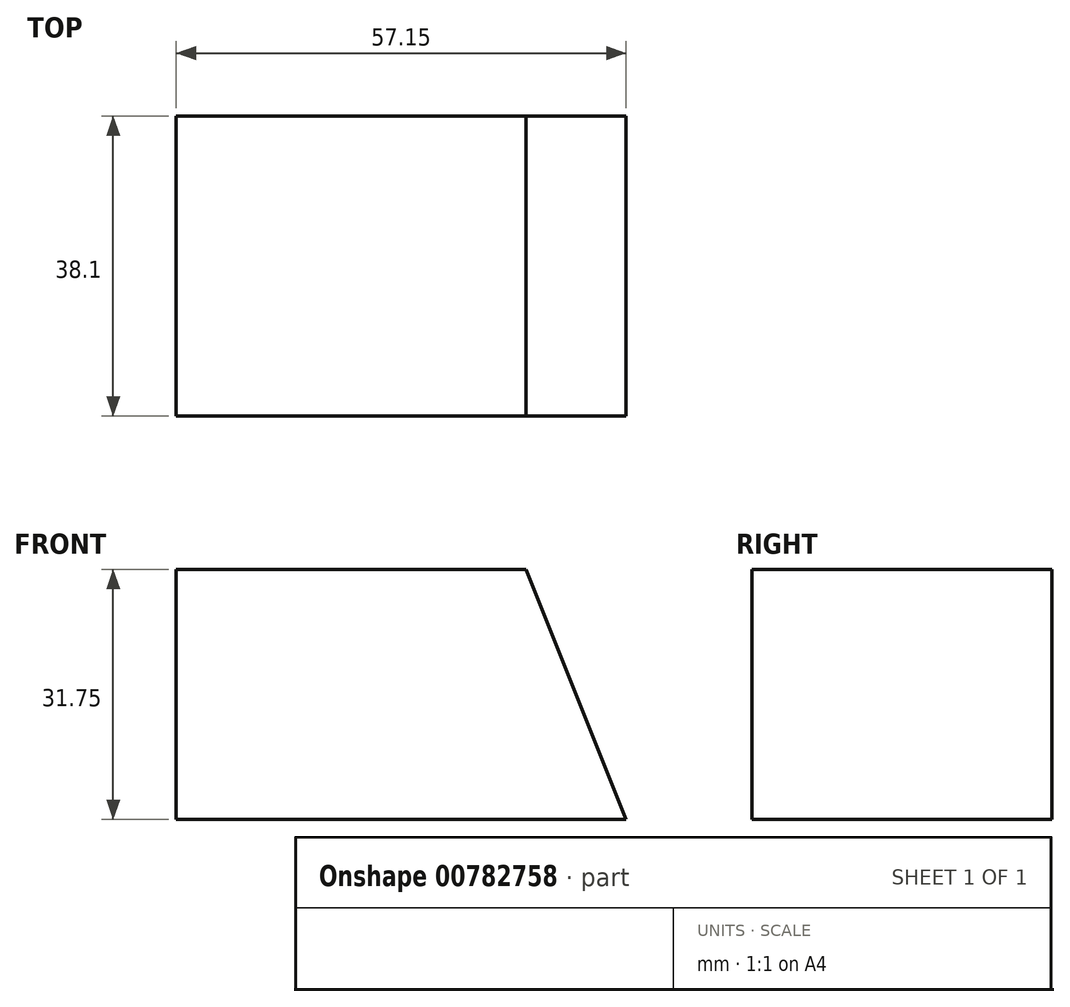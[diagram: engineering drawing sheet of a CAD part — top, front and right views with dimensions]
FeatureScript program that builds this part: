
annotation { "Feature Type Name" : "Feature", "Feature Type Description" : "" }
export const myFeature = defineFeature(function(context is Context, id is Id, definition is map)
    precondition{}
    {
        {
            var Q0;
            Q0=qCreatedBy(makeId("Front.planeOp"),FACE);
            var sketch = newSketch(context, id + "F0", { "sketchPlane" : qUnion([Q0])});
            skLineSegment(sketch, "E0", {"start": v(0, 0) * mm, "end": v(0, 31.75) * mm});
            skLineSegment(sketch, "E1", {"start": v(0, 31.75) * mm, "end": v(19.05, 31.75) * mm});
            skLineSegment(sketch, "E2", {"start": v(0, 0) * mm, "end": v(31.75, 0) * mm});
            skLineSegment(sketch, "E3", {"start": v(31.75, 0) * mm, "end": v(19.05, 31.75) * mm});
            skLineSegment(sketch, "E4", {"start": v(31.75, 0) * mm, "end": v(57.15, 0) * mm});
            skLineSegment(sketch, "E5", {"start": v(19.05, 31.75) * mm, "end": v(44.45, 31.75) * mm});
            skLineSegment(sketch, "E6", {"start": v(44.45, 31.75) * mm, "end": v(57.15, 0) * mm});
            skSolve(sketch);
        }
        {
            var Q0;
            Q0=makeQuery(id+"F0.imprint","IMPRINT",FACE,{"disambiguationData":[TD([[makeQuery(id+"F0.imprint","IMPRINT",EDGE,{"derivedFrom":sQuery(id+"F0.wireOp",EDGE,"E3")}),-1.0]])]});
            var Q1;
            Q1=makeQuery(id+"F0.imprint","IMPRINT",FACE,{"disambiguationData":[TD([[makeQuery(id+"F0.imprint","IMPRINT",EDGE,{"derivedFrom":sQuery(id+"F0.wireOp",EDGE,"E0")}),-1.0]])]});
            extrude(context, id + "F1", {"entities" : qUnion([Q0, Q1]), "depth" : 38.1 * mm, "offsetDistance" : 25.4 * mm});
        }
    });
